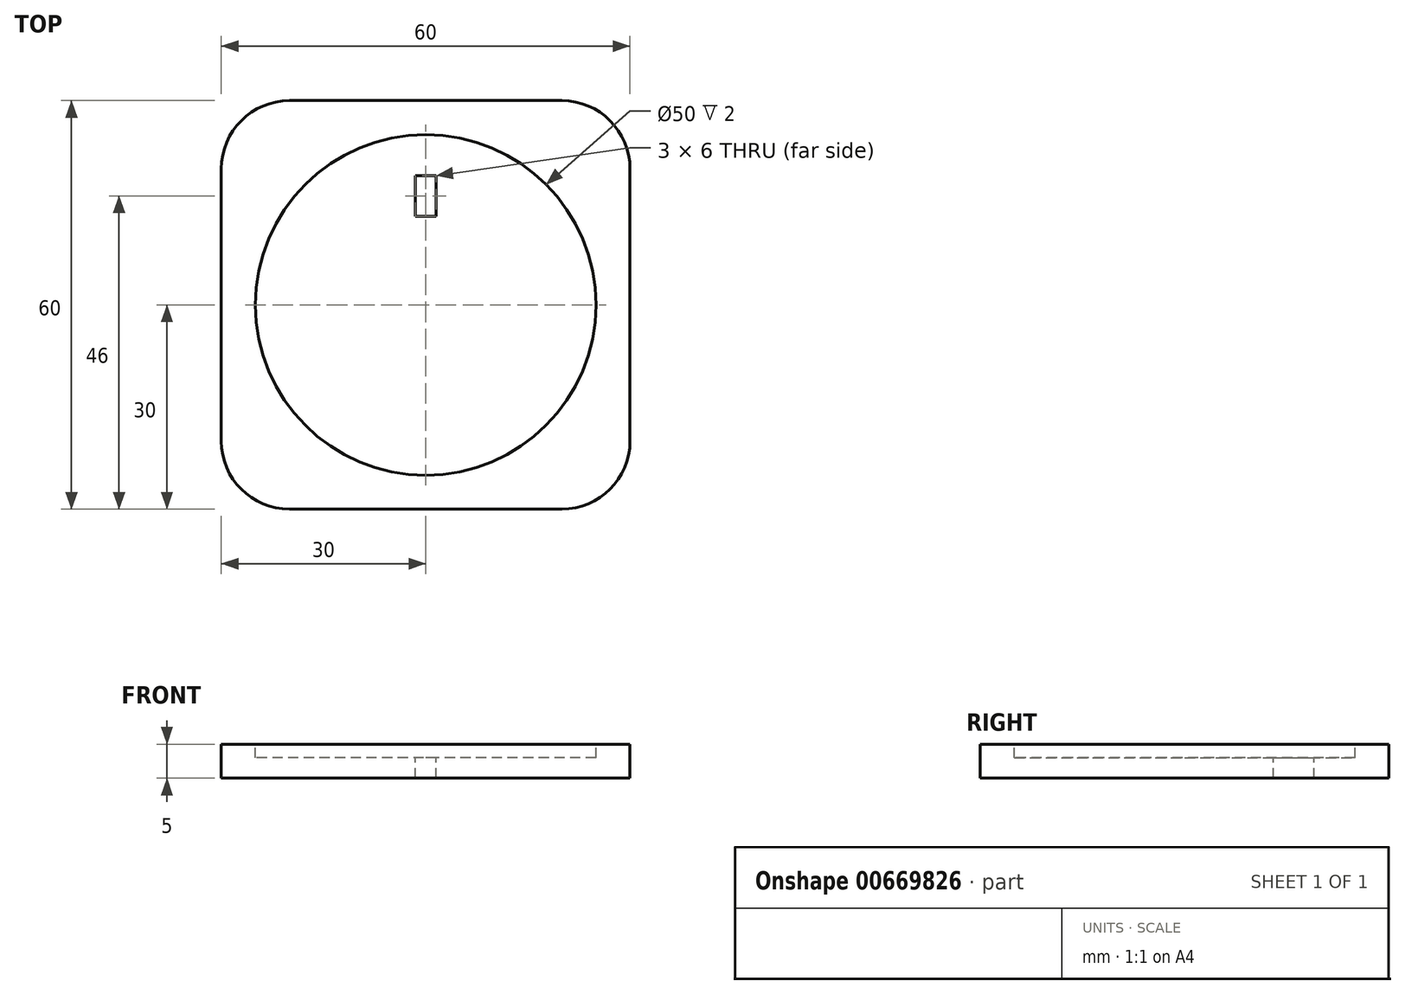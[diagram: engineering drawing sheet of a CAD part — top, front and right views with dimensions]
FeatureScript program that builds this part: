
annotation { "Feature Type Name" : "Feature", "Feature Type Description" : "" }
export const myFeature = defineFeature(function(context is Context, id is Id, definition is map)
    precondition{}
    {
        {
            var Q0;
            Q0=qCreatedBy(makeId("Top.planeOp"),FACE);
            var sketch = newSketch(context, id + "F0", { "sketchPlane" : qUnion([Q0])});
            skLineSegment(sketch, "E0.bottom", {"start": v(30, -30) * mm, "end": v(-30, -30) * mm});
            skLineSegment(sketch, "E0.top", {"start": v(30, 30) * mm, "end": v(-30, 30) * mm});
            skLineSegment(sketch, "E0.left", {"start": v(30, -30) * mm, "end": v(30, 30) * mm});
            skLineSegment(sketch, "E0.right", {"start": v(-30, -30) * mm, "end": v(-30, 30) * mm});
            skPoint(sketch, "E0.middle", {"position": v(0, 0) * mm});
            skSolve(sketch);
        }
        {
            var Q0;
            Q0=makeQuery(id+"F0.imprint","IMPRINT",FACE,{"disambiguationData":[TD([[makeQuery(id+"F0.imprint","IMPRINT",EDGE,{"derivedFrom":sQuery(id+"F0.wireOp",EDGE,"E0.bottom")}),-1.0]])]});
            var Q1;
            Q1 = qSketchRegion(id + "F2", true);
            extrude(context, id + "F1", {"entities" : qUnion([Q0, Q1]), "depth" : 5 * mm, "offsetDistance" : 25 * mm});
        }
        {
            var Q0;
            Q0=makeQuery(id+"F1.opExtrude","CAP_FACE",FACE,{"disambiguationData":[OSD([sQuery(id+"F0.wireOp",EDGE,"E0.bottom"),sQuery(id+"F0.wireOp",EDGE,"E0.top"),sQuery(id+"F0.wireOp",EDGE,"E0.left"),sQuery(id+"F0.wireOp",EDGE,"E0.right")])],"isStart":false});
            var sketch = newSketch(context, id + "F2", { "sketchPlane" : qUnion([Q0])});
            skCircle(sketch, "E1", {"center": v(0, 0) * mm, "radius": 25 * mm});
            skSolve(sketch);
        }
        {
            var Q0;
            Q0 = qSketchRegion(id + "F2", true);
            extrude(context, id + "F3", {"entities" : qUnion([Q0]), "operationType" : NewBodyOperationType.REMOVE, "oppositeDirection" : true, "depth" : 2 * mm, "offsetDistance" : 25 * mm});
        }
        {
            var Q0;
            Q0=makeQuery(id+"F1.opExtrude","SWEPT_EDGE",EDGE,{"disambiguationData":[OSD([sQuery(id+"F0.wireOp",EDGE,"E0.bottom"),sQuery(id+"F0.wireOp",EDGE,"E0.right")])]});
            var Q1;
            Q1=makeQuery(id+"F1.opExtrude","SWEPT_EDGE",EDGE,{"disambiguationData":[OSD([sQuery(id+"F0.wireOp",EDGE,"E0.bottom"),sQuery(id+"F0.wireOp",EDGE,"E0.left")])]});
            var Q2;
            Q2=makeQuery(id+"F1.opExtrude","SWEPT_EDGE",EDGE,{"disambiguationData":[OSD([sQuery(id+"F0.wireOp",EDGE,"E0.top"),sQuery(id+"F0.wireOp",EDGE,"E0.left")])]});
            var Q3;
            Q3=makeQuery(id+"F1.opExtrude","SWEPT_EDGE",EDGE,{"disambiguationData":[OSD([sQuery(id+"F0.wireOp",EDGE,"E0.top"),sQuery(id+"F0.wireOp",EDGE,"E0.right")])]});
            fillet(context, id + "F4", {"entities" : qUnion([Q0, Q1, Q2, Q3]), "radius" : 10 * mm, "tangentPropagation" : true, "allowEdgeOverflow" : false});
        }
        {
            var Q0;
            Q0=makeQuery(id+"F3.boolean.opBoolean","COPY",FACE,{"derivedFrom":makeQuery(id+"F3.opExtrude","CAP_FACE",FACE,{"disambiguationData":[OSD([sQuery(id+"F2.wireOp",EDGE,"E1")])],"isStart":false})});
            var sketch = newSketch(context, id + "F5", { "sketchPlane" : qUnion([Q0])});
            skLineSegment(sketch, "E2.bottom", {"start": v(1.5, 13) * mm, "end": v(-1.5, 13) * mm});
            skLineSegment(sketch, "E2.top", {"start": v(1.5, 19) * mm, "end": v(-1.5, 19) * mm});
            skLineSegment(sketch, "E2.left", {"start": v(1.5, 13) * mm, "end": v(1.5, 19) * mm});
            skLineSegment(sketch, "E2.right", {"start": v(-1.5, 13) * mm, "end": v(-1.5, 19) * mm});
            skPoint(sketch, "E2.middle", {"position": v(0, 16) * mm});
            skSolve(sketch);
        }
        {
            var Q0;
            Q0=makeQuery(id+"FvH0wHGysUMuku9_1.1.F5.imprint","IMPRINT",FACE,{"disambiguationData":[TD([[makeQuery(id+"FvH0wHGysUMuku9_1.1.F5.imprint","IMPRINT",EDGE,{"derivedFrom":sQuery(id+"FvH0wHGysUMuku9_1.1.F5.wireOp",EDGE,"E2.bottom")}),-1.0]])]});
            var Q1;
            Q1=makeQuery(id+"FvH0wHGysUMuku9_1.3.F5.imprint","IMPRINT",FACE,{"disambiguationData":[TD([[makeQuery(id+"FvH0wHGysUMuku9_1.3.F5.imprint","IMPRINT",EDGE,{"derivedFrom":sQuery(id+"FvH0wHGysUMuku9_1.3.F5.wireOp",EDGE,"E2.bottom")}),-1.0]])]});
            var Q2;
            Q2=makeQuery(id+"F5.imprint","IMPRINT",FACE,{"disambiguationData":[TD([[makeQuery(id+"F5.imprint","IMPRINT",EDGE,{"derivedFrom":sQuery(id+"F5.wireOp",EDGE,"E2.bottom")}),-1.0]])]});
            var Q3;
            Q3=makeQuery(id+"FvH0wHGysUMuku9_1.2.F5.imprint","IMPRINT",FACE,{"disambiguationData":[TD([[makeQuery(id+"FvH0wHGysUMuku9_1.2.F5.imprint","IMPRINT",EDGE,{"derivedFrom":sQuery(id+"FvH0wHGysUMuku9_1.2.F5.wireOp",EDGE,"E2.bottom")}),-1.0]])]});
            extrude(context, id + "F6", {"entities" : qUnion([Q0, Q1, Q2, Q3]), "operationType" : NewBodyOperationType.REMOVE, "oppositeDirection" : true, "depth" : 25 * mm, "offsetDistance" : 25 * mm});
        }
    });
